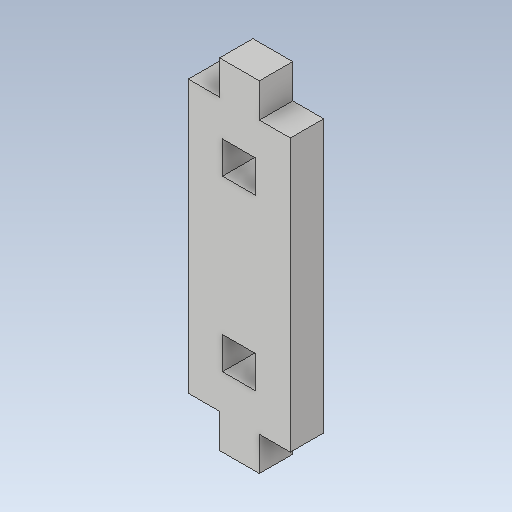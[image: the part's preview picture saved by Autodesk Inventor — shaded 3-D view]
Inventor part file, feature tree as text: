
AUTODESK INVENTOR PART (.ipt)
format: ipt  version: 2020 (Build 240168000, 168)  size: 113,152 bytes
history: native  units: mm
features: other x1, extrude x1, sketch x1
ambient origin geometry x8: Origin, YZ Plane, XZ Plane, XY Plane, X Axis, Y Axis, Z Axis, Center Point
bodies: Body1 (feature_tree)
feature tree (3):
  other  "Твердое тело1"
  extrude  "Выдавливание1"  Depth=4.9mm TaperAngle=0.0deg
  sketch  "Эскиз1"
